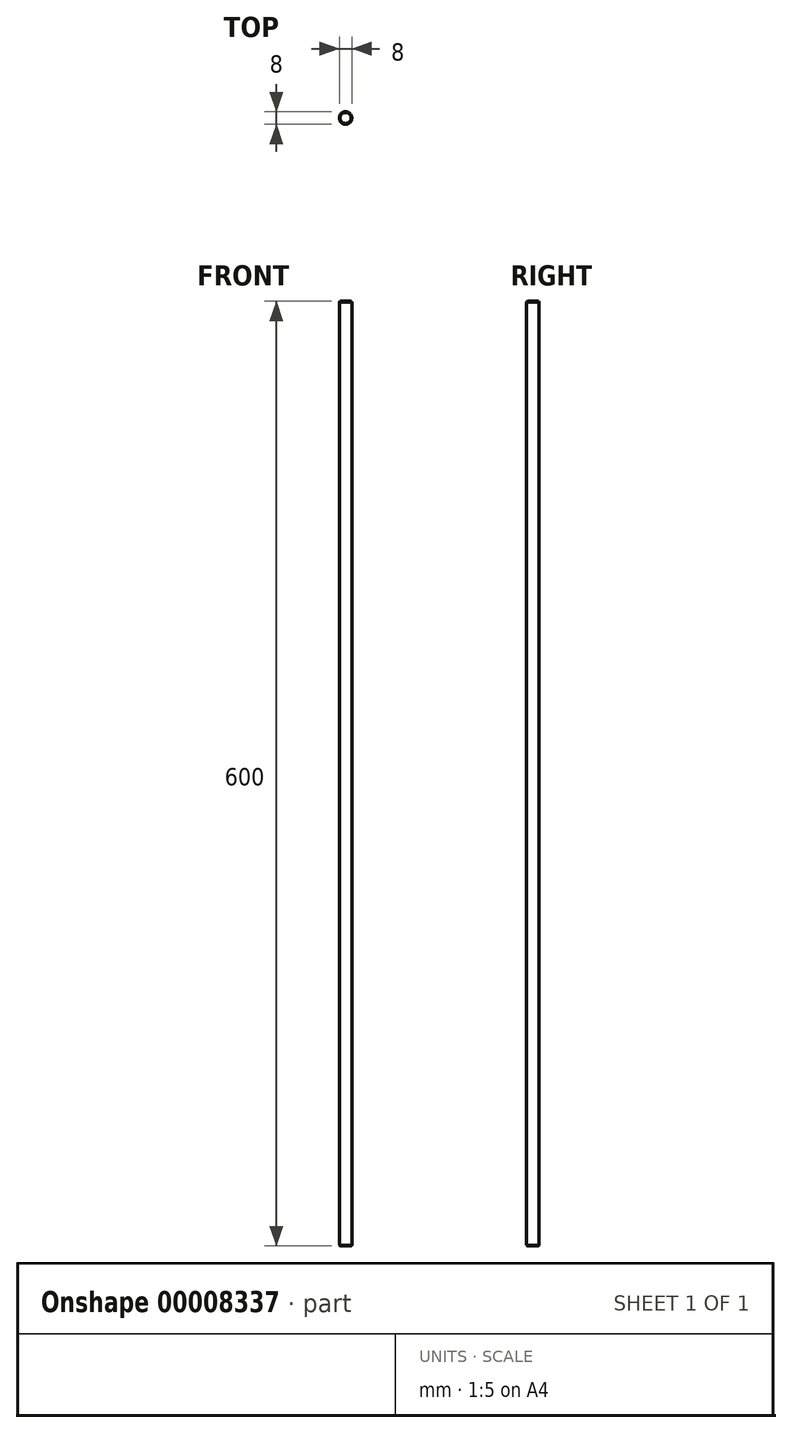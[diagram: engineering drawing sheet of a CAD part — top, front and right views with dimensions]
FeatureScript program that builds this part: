
annotation { "Feature Type Name" : "Feature", "Feature Type Description" : "" }
export const myFeature = defineFeature(function(context is Context, id is Id, definition is map)
    precondition{}
    {
        {
            var Q0;
            Q0=qCreatedBy(makeId("Top.planeOp"),FACE);
            var sketch = newSketch(context, id + "F0", { "sketchPlane" : qUnion([Q0])});
            skCircle(sketch, "E0", {"center": v(0, 0) * mm, "radius": 4 * mm});
            skSolve(sketch);
        }
        {
            var Q0;
            Q0 = qSketchRegion(id + "F0", true);
            extrude(context, id + "F1", {"entities" : qUnion([Q0]), "depth" : 600 * mm});
        }
        {
            var Q0;
            Q0=makeQuery(id+"F1.opExtrude","CAP_EDGE",EDGE,{"disambiguationData":[OSD([sQuery(id+"F0.wireOp",EDGE,"E0")])],"isStart":true});
            var Q1;
            Q1=makeQuery(id+"F1.opExtrude","CAP_EDGE",EDGE,{"disambiguationData":[OSD([sQuery(id+"F0.wireOp",EDGE,"E0")])],"isStart":false});
            chamfer(context, id + "F2", {"entities" : qUnion([Q0, Q1]), "width" : 0.5 * mm, "tangentPropagation" : true});
        }
    });
